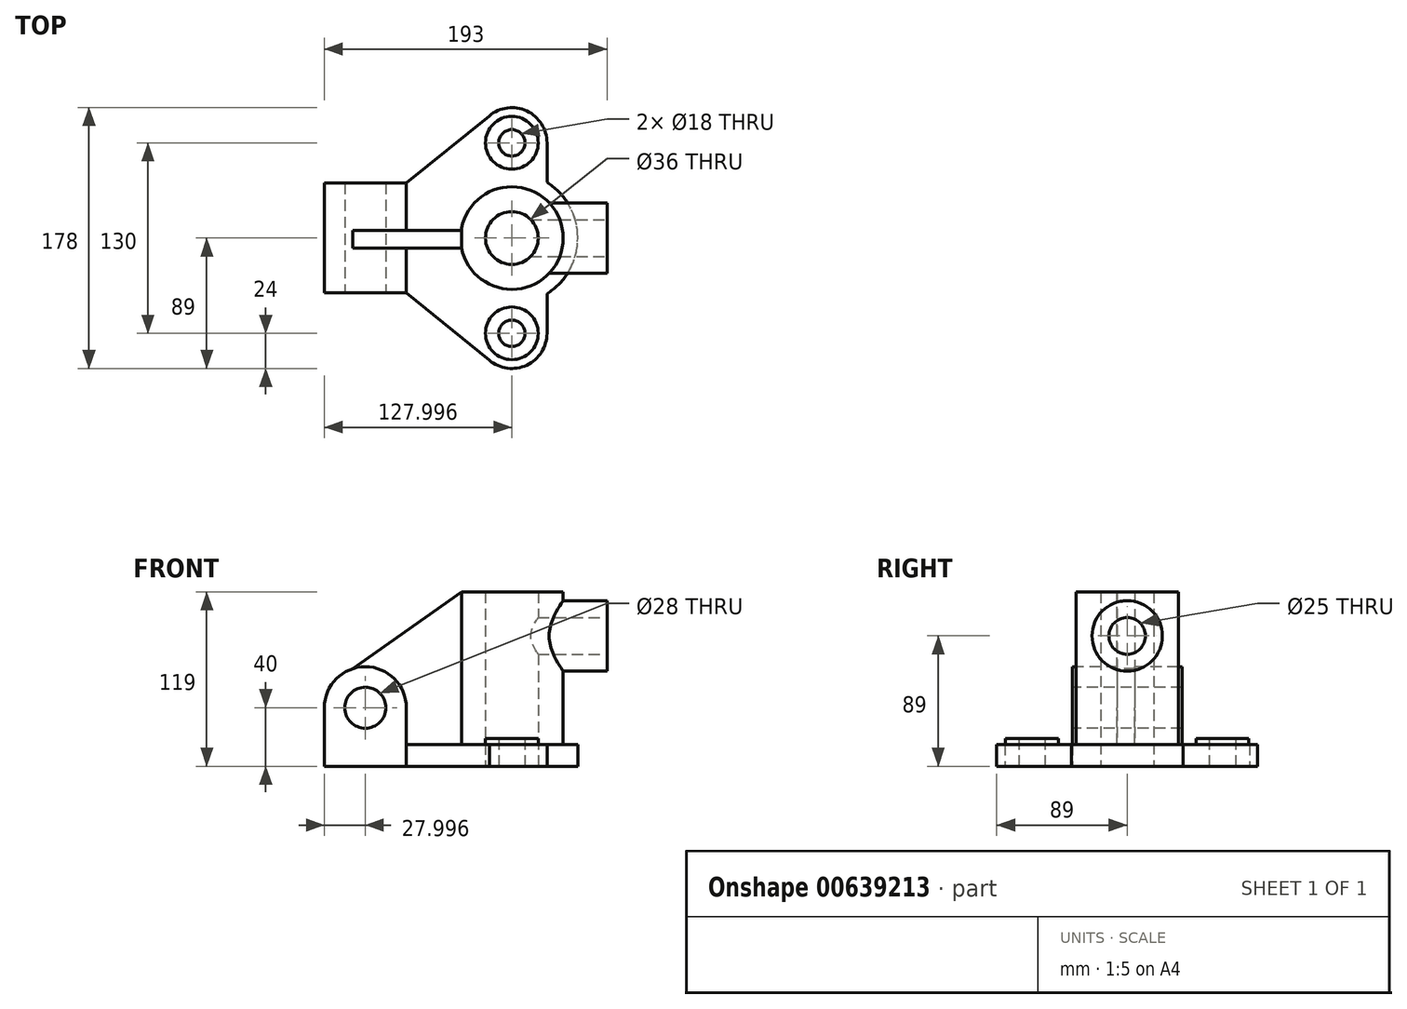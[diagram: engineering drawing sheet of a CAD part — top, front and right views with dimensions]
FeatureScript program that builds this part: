
annotation { "Feature Type Name" : "Feature", "Feature Type Description" : "" }
export const myFeature = defineFeature(function(context is Context, id is Id, definition is map)
    precondition{}
    {
        {
            var Q0;
            Q0=qCreatedBy(makeId("Top.planeOp"),FACE);
            var sketch = newSketch(context, id + "F0", { "sketchPlane" : qUnion([Q0])});
            skLineSegment(sketch, "E0.bottom", {"start": v(-72.27, 37.5) * mm, "end": v(-16.27, 37.5) * mm});
            skLineSegment(sketch, "E0.top", {"start": v(-72.27, -37.5) * mm, "end": v(-16.27, -37.5) * mm});
            skLineSegment(sketch, "E0.left", {"start": v(-72.27, 37.5) * mm, "end": v(-72.27, -37.5) * mm});
            skLineSegment(sketch, "E1.right", {"start": v(120.73, 69.04) * mm, "end": v(120.73, -71.76) * mm});
            skLineSegment(sketch, "E2", {"start": v(55.73, 65) * mm, "end": v(55.73, -65) * mm});
            skCircle(sketch, "E3", {"center": v(55.73, 0) * mm, "radius": 18 * mm});
            skCircle(sketch, "E4", {"center": v(55.73, 0) * mm, "radius": 35 * mm});
            skCircle(sketch, "E5", {"center": v(55.73, 65) * mm, "radius": 9 * mm});
            skCircle(sketch, "E6", {"center": v(55.73, 65) * mm, "radius": 18 * mm});
            skCircle(sketch, "E7", {"center": v(55.73, -65) * mm, "radius": 9 * mm});
            skCircle(sketch, "E8", {"center": v(55.73, -65) * mm, "radius": 18 * mm});
            skLineSegment(sketch, "E9.bottom", {"start": v(55.73, 65) * mm, "end": v(55.73, 65) * mm});
            skLineSegment(sketch, "E9.top", {"start": v(55.73, -65) * mm, "end": v(55.73, -65) * mm});
            skLineSegment(sketch, "E10.bottom", {"start": v(120.73, -65) * mm, "end": v(55.73, -65) * mm});
            skLineSegment(sketch, "E10.left", {"start": v(120.73, -65) * mm, "end": v(120.73, 65) * mm});
            skArc(sketch, "E11", {"start": v(79.73, 38.07) * mm, "mid": v(100.73, 0) * mm, "end": v(79.73, -38.07) * mm});
            skLineSegment(sketch, "E12", {"start": v(79.73, 65) * mm, "end": v(79.73, 38.07) * mm});
            skArc(sketch, "E13", {"start": v(79.73, -65) * mm, "mid": v(72.7, -81.97) * mm, "end": v(55.73, -89) * mm});
            skArc(sketch, "E14", {"start": v(79.73, 65) * mm, "mid": v(72.7, 81.97) * mm, "end": v(55.73, 89) * mm});
            skArc(sketch, "E15", {"start": v(55.73, 89) * mm, "mid": v(47.56, 87.57) * mm, "end": v(40.37, 83.44) * mm});
            skArc(sketch, "E16", {"start": v(55.73, -89) * mm, "mid": v(47.56, -87.57) * mm, "end": v(40.37, -83.44) * mm});
            skLineSegment(sketch, "E17", {"start": v(40.37, 83.44) * mm, "end": v(-16.27, 37.5) * mm});
            skLineSegment(sketch, "E18", {"start": v(-16.27, -37.5) * mm, "end": v(40.37, -83.44) * mm});
            skLineSegment(sketch, "E19", {"start": v(79.73, -38.07) * mm, "end": v(79.73, -65) * mm});
            skLineSegment(sketch, "E20", {"start": v(-16.27, 37.5) * mm, "end": v(-16.27, -37.5) * mm});
            skSolve(sketch);
        }
        {
            var Q0;
            Q0=makeQuery(id+"F0.imprint","IMPRINT",FACE,{"disambiguationData":[TD([[makeQuery(id+"F0.imprint","IMPRINT",EDGE,{"derivedFrom":sQuery(id+"F0.wireOp",EDGE,"E0.bottom")}),-1.0]])]});
            extrude(context, id + "F1", {"entities" : qUnion([Q0]), "depth" : 40 * mm, "offsetDistance" : 25 * mm});
        }
        {
            var Q0;
            Q0=makeQuery(id+"F1.opExtrude","SWEPT_FACE",FACE,{"disambiguationData":[OSD([sQuery(id+"F0.wireOp",EDGE,"E0.top")])]});
            var sketch = newSketch(context, id + "F2", { "sketchPlane" : qUnion([Q0])});
            skArc(sketch, "E21", {"start": v(-16.27, 40) * mm, "mid": v(-44.27, 68) * mm, "end": v(-72.27, 40) * mm});
            skLineSegment(sketch, "E22", {"start": v(-16.27, 40) * mm, "end": v(-72.27, 40) * mm});
            skCircle(sketch, "E23", {"center": v(-44.27, 40) * mm, "radius": 14 * mm});
            skSolve(sketch);
        }
        {
            var Q0;
            Q0=makeQuery(id+"F2.imprint","IMPRINT",FACE,{"disambiguationData":[TD([[makeQuery(id+"F2.imprint","IMPRINT",EDGE,{"derivedFrom":sQuery(id+"F2.wireOp",EDGE,"E21")}),1.0]])]});
            extrude(context, id + "F3", {"entities" : qUnion([Q0]), "operationType" : NewBodyOperationType.ADD, "oppositeDirection" : true, "depth" : 75 * mm, "offsetDistance" : 25 * mm});
        }
        {
            var Q0;
            Q0=makeQuery(id+"F0.imprint","IMPRINT",FACE,{"disambiguationData":[TD([[makeQuery(id+"F0.imprint","IMPRINT",EDGE,{"derivedFrom":sQuery(id+"F0.wireOp",EDGE,"E6")}),-1.0]])]});
            extrude(context, id + "F4", {"entities" : qUnion([Q0]), "operationType" : NewBodyOperationType.ADD, "depth" : 15 * mm, "offsetDistance" : 25 * mm});
        }
        {
            var Q0;
            Q0=makeQuery(id+"F0.imprint","IMPRINT",FACE,{"disambiguationData":[TD([[makeQuery(id+"F0.imprint","IMPRINT",EDGE,{"derivedFrom":sQuery(id+"F0.wireOp",EDGE,"E5")}),-1.0]])]});
            var Q1;
            {var subQ0=sQuery(id+"F0.wireOp",EDGE,"E2");var subQ1=sQuery(id+"F0.wireOp",EDGE,"E7");var subQ2=makeQuery(id+"F0.imprint","INTERSECT",VERTEX,{"derivedFrom":[subQ1,subQ0]});Q1=makeQuery(id+"F0.imprint","IMPRINT",FACE,{"disambiguationData":[TD([[makeQuery(id+"F0.imprint","IMPRINT",EDGE,{"disambiguationData":[TD([[subQ2,1.0]])],"derivedFrom":subQ1}),-1.0]])]});}
            var Q2;
            {var subQ0=sQuery(id+"F0.wireOp",EDGE,"E2");var subQ1=sQuery(id+"F0.wireOp",EDGE,"E7");var subQ2=makeQuery(id+"F0.imprint","INTERSECT",VERTEX,{"derivedFrom":[subQ1,subQ0]});Q2=makeQuery(id+"F0.imprint","IMPRINT",FACE,{"disambiguationData":[TD([[makeQuery(id+"F0.imprint","IMPRINT",EDGE,{"disambiguationData":[TD([[subQ2,-1.0]])],"derivedFrom":subQ1}),-1.0]])]});}
            extrude(context, id + "F5", {"entities" : qUnion([Q0, Q1, Q2]), "operationType" : NewBodyOperationType.ADD, "depth" : 19 * mm, "offsetDistance" : 25 * mm});
        }
        {
            var Q0;
            {var subQ0=sQuery(id+"F0.wireOp",EDGE,"E2");var subQ1=sQuery(id+"F0.wireOp",EDGE,"E3");var subQ2=makeQuery(id+"F0.imprint","INTERSECT",VERTEX,{"disambiguationData":[OD(0.0)],"derivedFrom":[subQ1,subQ0]});Q0=makeQuery(id+"F0.imprint","IMPRINT",FACE,{"disambiguationData":[TD([[makeQuery(id+"F0.imprint","IMPRINT",EDGE,{"disambiguationData":[TD([[subQ2,1.0]])],"derivedFrom":subQ1}),-1.0]])]});}
            var Q1;
            {var subQ0=sQuery(id+"F0.wireOp",EDGE,"E2");var subQ1=sQuery(id+"F0.wireOp",EDGE,"E3");var subQ2=makeQuery(id+"F0.imprint","INTERSECT",VERTEX,{"disambiguationData":[OD(0.0)],"derivedFrom":[subQ1,subQ0]});Q1=makeQuery(id+"F0.imprint","IMPRINT",FACE,{"disambiguationData":[TD([[makeQuery(id+"F0.imprint","IMPRINT",EDGE,{"disambiguationData":[TD([[subQ2,-1.0]])],"derivedFrom":subQ1}),-1.0]])]});}
            extrude(context, id + "F6", {"entities" : qUnion([Q0, Q1]), "operationType" : NewBodyOperationType.ADD, "depth" : 119 * mm, "offsetDistance" : 25 * mm});
        }
        {
            var Q0;
            Q0=makeQuery(id+"F4.opExtrude","CAP_FACE",FACE,{"disambiguationData":[OSD([sQuery(id+"F0.wireOp",EDGE,"E4"),sQuery(id+"F0.wireOp",EDGE,"E6"),sQuery(id+"F0.wireOp",EDGE,"E8"),sQuery(id+"F0.wireOp",EDGE,"E11"),sQuery(id+"F0.wireOp",EDGE,"E12"),sQuery(id+"F0.wireOp",EDGE,"E13"),sQuery(id+"F0.wireOp",EDGE,"E14"),sQuery(id+"F0.wireOp",EDGE,"E15"),sQuery(id+"F0.wireOp",EDGE,"E16"),sQuery(id+"F0.wireOp",EDGE,"E17"),sQuery(id+"F0.wireOp",EDGE,"E18"),sQuery(id+"F0.wireOp",EDGE,"E19"),sQuery(id+"F0.wireOp",EDGE,"E20")])],"isStart":false});
            var sketch = newSketch(context, id + "F7", { "sketchPlane" : qUnion([Q0])});
            skLineSegment(sketch, "E24.bottom", {"start": v(-66.6, 5.19) * mm, "end": v(21.4, 5.19) * mm});
            skLineSegment(sketch, "E24.top", {"start": v(-66.6, -6.81) * mm, "end": v(21.4, -6.81) * mm});
            skLineSegment(sketch, "E24.left", {"start": v(-66.6, 5.19) * mm, "end": v(-66.6, -6.81) * mm});
            skLineSegment(sketch, "E24.right", {"start": v(21.4, 5.19) * mm, "end": v(21.4, -6.81) * mm});
            skSolve(sketch);
        }
        {
            var Q0;
            Q0 = qSketchRegion(id + "F7", true);
            extrude(context, id + "F8", {"entities" : qUnion([Q0]), "operationType" : NewBodyOperationType.ADD, "depth" : 104 * mm, "offsetDistance" : 25 * mm});
        }
        {
            var Q0;
            Q0=makeQuery(id+"F8.opExtrude","SWEPT_FACE",FACE,{"disambiguationData":[OSD([sQuery(id+"F7.wireOp",EDGE,"E24.top")])]});
            var sketch = newSketch(context, id + "F9", { "sketchPlane" : qUnion([Q0])});
            skLineSegment(sketch, "E25", {"start": v(21.4, 119) * mm, "end": v(-66.6, 119) * mm});
            skLineSegment(sketch, "E26", {"start": v(-66.6, 119) * mm, "end": v(-66.6, 56.9) * mm});
            skLineSegment(sketch, "E27", {"start": v(-66.6, 56.9) * mm, "end": v(21.4, 119) * mm});
            skSolve(sketch);
        }
        {
            var Q0;
            {var subQ0=sQuery(id+"F9.wireOp",EDGE,"E25");Q0=makeQuery(id+"F9.imprint","IMPRINT",FACE,{"disambiguationData":[TD([[makeQuery(id+"F9.imprint","IMPRINT",EDGE,{"derivedFrom":subQ0}),-1.0]])]});}
            extrude(context, id + "F10", {"entities" : qUnion([Q0]), "operationType" : NewBodyOperationType.REMOVE, "oppositeDirection" : true, "depth" : 25 * mm, "offsetDistance" : 25 * mm});
        }
        {
            var Q0;
            {var subQ0=sQuery(id+"F2.wireOp",EDGE,"E23");var subQ1=sQuery(id+"F2.wireOp",EDGE,"E22");var subQ2=makeQuery(id+"F2.imprint","INTERSECT",VERTEX,{"disambiguationData":[OD(0.0)],"derivedFrom":[subQ1,subQ0]});Q0=makeQuery(id+"F2.imprint","IMPRINT",FACE,{"disambiguationData":[TD([[makeQuery(id+"F2.imprint","IMPRINT",EDGE,{"disambiguationData":[TD([[subQ2,-1.0]])],"derivedFrom":subQ1}),1.0]])]});}
            var Q1;
            {var subQ0=sQuery(id+"F2.wireOp",EDGE,"E23");var subQ1=sQuery(id+"F2.wireOp",EDGE,"E22");var subQ2=makeQuery(id+"F2.imprint","INTERSECT",VERTEX,{"disambiguationData":[OD(0.0)],"derivedFrom":[subQ1,subQ0]});Q1=makeQuery(id+"F2.imprint","IMPRINT",FACE,{"disambiguationData":[TD([[makeQuery(id+"F2.imprint","IMPRINT",EDGE,{"disambiguationData":[TD([[subQ2,-1.0]])],"derivedFrom":subQ1}),-1.0]])]});}
            extrude(context, id + "F11", {"entities" : qUnion([Q0, Q1]), "operationType" : NewBodyOperationType.REMOVE, "oppositeDirection" : true, "depth" : 75 * mm, "offsetDistance" : 25 * mm});
        }
        {
            var Q0;
            Q0=makeQuery(id+"F4.opExtrude","SWEPT_FACE",FACE,{"disambiguationData":[OSD([sQuery(id+"F0.wireOp",EDGE,"E12")])]});
            var sketch = newSketch(context, id + "F12", { "sketchPlane" : qUnion([Q0])});
            skCircle(sketch, "E28", {"center": v(0, 89) * mm, "radius": 12.5 * mm});
            skSolve(sketch);
        }
        {
            var Q0;
            Q0 = qSketchRegion(id + "F12", true);
            extrude(context, id + "F13", {"entities" : qUnion([Q0]), "operationType" : NewBodyOperationType.REMOVE, "oppositeDirection" : true, "depth" : 25 * mm, "offsetDistance" : 25 * mm, "symmetric" : true});
        }
        {
            var Q0;
            Q0=makeQuery(id+"F4.opExtrude","SWEPT_FACE",FACE,{"disambiguationData":[OSD([sQuery(id+"F0.wireOp",EDGE,"E12")])]});
            var sketch = newSketch(context, id + "F14", { "sketchPlane" : qUnion([Q0])});
            skCircle(sketch, "E29", {"center": v(0, 89) * mm, "radius": 24 * mm});
            skCircle(sketch, "E30", {"center": v(0, 89) * mm, "radius": 12.5 * mm});
            skSolve(sketch);
        }
        {
            var Q0;
            Q0 = qSketchRegion(id + "F14", true);
            extrude(context, id + "F15", {"entities" : qUnion([Q0]), "operationType" : NewBodyOperationType.ADD, "depth" : 41 * mm, "offsetDistance" : 25 * mm});
        }
    });
